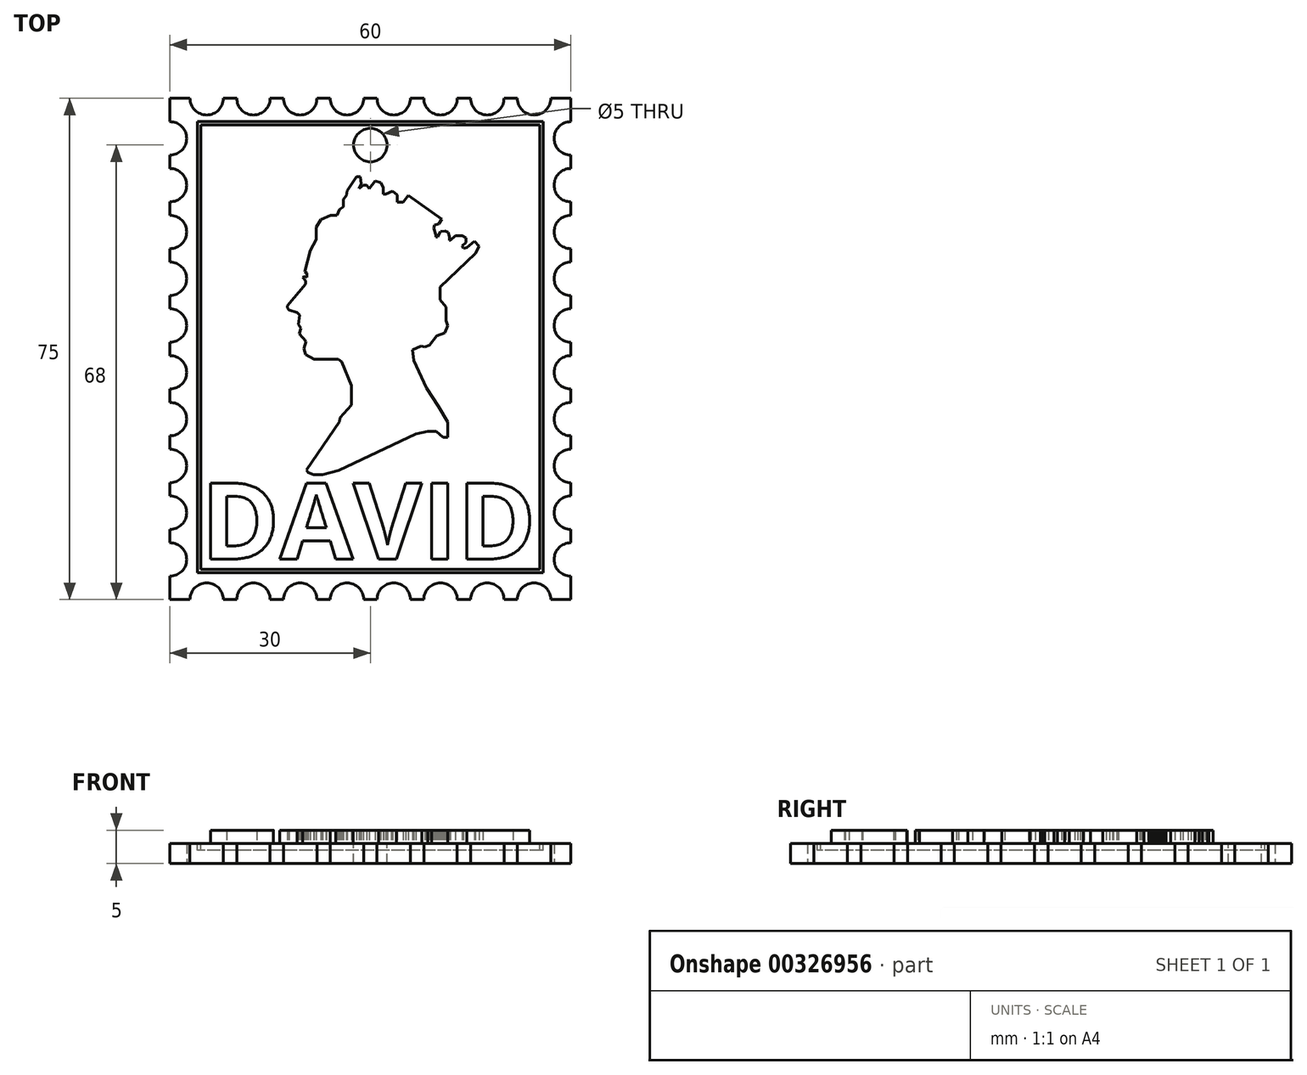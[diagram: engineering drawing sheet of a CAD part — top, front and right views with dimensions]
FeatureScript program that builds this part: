
annotation { "Feature Type Name" : "Feature", "Feature Type Description" : "" }
export const myFeature = defineFeature(function(context is Context, id is Id, definition is map)
    precondition{}
    {
        {
            var Q0;
            Q0=qCreatedBy(makeId("Top.planeOp"),FACE);
            var sketch = newSketch(context, id + "F0", { "sketchPlane" : qUnion([Q0])});
            skLineSegment(sketch, "E0.bottom", {"start": v(30, 37.5) * mm, "end": v(27, 37.5) * mm});
            skLineSegment(sketch, "E0.top", {"start": v(30, -37.5) * mm, "end": v(27, -37.5) * mm});
            skLineSegment(sketch, "E0.left", {"start": v(30, 37.5) * mm, "end": v(30, 34) * mm});
            skLineSegment(sketch, "E0.right", {"start": v(-30, 37.5) * mm, "end": v(-30, 34) * mm});
            skPoint(sketch, "E0.middle", {"position": v(0, 0) * mm});
            skArc(sketch, "E1", {"start": v(-27, 37.5) * mm, "mid": v(-24.5, 35) * mm, "end": v(-22, 37.5) * mm});
            skArc(sketch, "E2.1.0.0", {"start": v(-20, 37.5) * mm, "mid": v(-17.5, 35) * mm, "end": v(-15, 37.5) * mm});
            skArc(sketch, "E2.2.0.0", {"start": v(-13, 37.5) * mm, "mid": v(-10.5, 35) * mm, "end": v(-8, 37.5) * mm});
            skArc(sketch, "E2.3.0.0", {"start": v(-6, 37.5) * mm, "mid": v(-3.5, 35) * mm, "end": v(-1, 37.5) * mm});
            skArc(sketch, "E2.4.0.0", {"start": v(1, 37.5) * mm, "mid": v(3.5, 35) * mm, "end": v(6, 37.5) * mm});
            skArc(sketch, "E2.5.0.0", {"start": v(8, 37.5) * mm, "mid": v(10.5, 35) * mm, "end": v(13, 37.5) * mm});
            skArc(sketch, "E2.6.0.0", {"start": v(15, 37.5) * mm, "mid": v(17.5, 35) * mm, "end": v(20, 37.5) * mm});
            skArc(sketch, "E2.7.0.0", {"start": v(22, 37.5) * mm, "mid": v(24.5, 35) * mm, "end": v(27, 37.5) * mm});
            skLineSegment(sketch, "E2.direction1", {"start": v(-22, 37.5) * mm, "end": v(-20, 37.5) * mm, "construction": true});
            skArc(sketch, "E3", {"start": v(-30, 29) * mm, "mid": v(-27.5, 31.5) * mm, "end": v(-30, 34) * mm});
            skArc(sketch, "E4.0.1.0", {"start": v(-30, 22) * mm, "mid": v(-27.5, 24.5) * mm, "end": v(-30, 27) * mm});
            skArc(sketch, "E4.0.2.0", {"start": v(-30, 15) * mm, "mid": v(-27.5, 17.5) * mm, "end": v(-30, 20) * mm});
            skArc(sketch, "E4.0.3.0", {"start": v(-30, 8) * mm, "mid": v(-27.5, 10.5) * mm, "end": v(-30, 13) * mm});
            skArc(sketch, "E4.0.4.0", {"start": v(-30, 1) * mm, "mid": v(-27.5, 3.5) * mm, "end": v(-30, 6) * mm});
            skArc(sketch, "E4.0.5.0", {"start": v(-30, -6) * mm, "mid": v(-27.5, -3.5) * mm, "end": v(-30, -1) * mm});
            skArc(sketch, "E4.0.6.0", {"start": v(-30, -13) * mm, "mid": v(-27.5, -10.5) * mm, "end": v(-30, -8) * mm});
            skArc(sketch, "E4.0.7.0", {"start": v(-30, -20) * mm, "mid": v(-27.5, -17.5) * mm, "end": v(-30, -15) * mm});
            skArc(sketch, "E4.0.8.0", {"start": v(-30, -27) * mm, "mid": v(-27.5, -24.5) * mm, "end": v(-30, -22) * mm});
            skArc(sketch, "E4.0.9.0", {"start": v(-30, -34) * mm, "mid": v(-27.5, -31.5) * mm, "end": v(-30, -29) * mm});
            skArc(sketch, "E4.1.1.0", {"start": v(-30, 22) * mm, "mid": v(-27.5, 24.5) * mm, "end": v(-30, 27) * mm});
            skArc(sketch, "E4.1.2.0", {"start": v(-30, 15) * mm, "mid": v(-27.5, 17.5) * mm, "end": v(-30, 20) * mm});
            skArc(sketch, "E4.1.3.0", {"start": v(-30, 8) * mm, "mid": v(-27.5, 10.5) * mm, "end": v(-30, 13) * mm});
            skArc(sketch, "E4.1.4.0", {"start": v(-30, 1) * mm, "mid": v(-27.5, 3.5) * mm, "end": v(-30, 6) * mm});
            skArc(sketch, "E4.1.5.0", {"start": v(-30, -6) * mm, "mid": v(-27.5, -3.5) * mm, "end": v(-30, -1) * mm});
            skArc(sketch, "E4.1.6.0", {"start": v(-30, -13) * mm, "mid": v(-27.5, -10.5) * mm, "end": v(-30, -8) * mm});
            skArc(sketch, "E4.1.7.0", {"start": v(-30, -20) * mm, "mid": v(-27.5, -17.5) * mm, "end": v(-30, -15) * mm});
            skArc(sketch, "E4.1.8.0", {"start": v(-30, -27) * mm, "mid": v(-27.5, -24.5) * mm, "end": v(-30, -22) * mm});
            skArc(sketch, "E4.1.9.0", {"start": v(-30, -34) * mm, "mid": v(-27.5, -31.5) * mm, "end": v(-30, -29) * mm});
            skArc(sketch, "E4.2.1.0", {"start": v(-30, 22) * mm, "mid": v(-27.5, 24.5) * mm, "end": v(-30, 27) * mm});
            skArc(sketch, "E4.2.2.0", {"start": v(-30, 15) * mm, "mid": v(-27.5, 17.5) * mm, "end": v(-30, 20) * mm});
            skArc(sketch, "E4.2.3.0", {"start": v(-30, 8) * mm, "mid": v(-27.5, 10.5) * mm, "end": v(-30, 13) * mm});
            skArc(sketch, "E4.2.4.0", {"start": v(-30, 1) * mm, "mid": v(-27.5, 3.5) * mm, "end": v(-30, 6) * mm});
            skArc(sketch, "E4.2.5.0", {"start": v(-30, -6) * mm, "mid": v(-27.5, -3.5) * mm, "end": v(-30, -1) * mm});
            skArc(sketch, "E4.2.6.0", {"start": v(-30, -13) * mm, "mid": v(-27.5, -10.5) * mm, "end": v(-30, -8) * mm});
            skArc(sketch, "E4.2.7.0", {"start": v(-30, -20) * mm, "mid": v(-27.5, -17.5) * mm, "end": v(-30, -15) * mm});
            skArc(sketch, "E4.2.9.0", {"start": v(-30, -34) * mm, "mid": v(-27.5, -31.5) * mm, "end": v(-30, -29) * mm});
            skLineSegment(sketch, "E4.direction1", {"start": v(-30, 31.5) * mm, "end": v(-30, 31.5) * mm});
            skLineSegment(sketch, "E4.direction2", {"start": v(-30, 29) * mm, "end": v(-30, 27) * mm, "construction": true});
            skLineSegment(sketch, "E5.trimOffspring", {"start": v(-27, 37.5) * mm, "end": v(-30, 37.5) * mm});
            skLineSegment(sketch, "E6.trimOffspring", {"start": v(-20, 37.5) * mm, "end": v(-22, 37.5) * mm});
            skLineSegment(sketch, "E7.trimOffspring", {"start": v(-13, 37.5) * mm, "end": v(-15, 37.5) * mm});
            skLineSegment(sketch, "E8.trimOffspring", {"start": v(-6, 37.5) * mm, "end": v(-8, 37.5) * mm});
            skLineSegment(sketch, "E9.trimOffspring", {"start": v(1, 37.5) * mm, "end": v(-1, 37.5) * mm});
            skLineSegment(sketch, "E10.trimOffspring", {"start": v(8, 37.5) * mm, "end": v(6, 37.5) * mm});
            skLineSegment(sketch, "E11.trimOffspring", {"start": v(15, 37.5) * mm, "end": v(13, 37.5) * mm});
            skLineSegment(sketch, "E12.trimOffspring", {"start": v(22, 37.5) * mm, "end": v(20, 37.5) * mm});
            skLineSegment(sketch, "E13.trimOffspring", {"start": v(-30, 29) * mm, "end": v(-30, 24.5) * mm});
            skLineSegment(sketch, "E14.trimOffspring", {"start": v(-30, 22) * mm, "end": v(-30, 20) * mm});
            skLineSegment(sketch, "E15.trimOffspring", {"start": v(-30, 15) * mm, "end": v(-30, 13) * mm});
            skLineSegment(sketch, "E16.trimOffspring", {"start": v(-30, 8) * mm, "end": v(-30, 6) * mm});
            skLineSegment(sketch, "E17.trimOffspring", {"start": v(-30, 1) * mm, "end": v(-30, -1) * mm});
            skLineSegment(sketch, "E18.trimOffspring", {"start": v(-30, -6) * mm, "end": v(-30, -8) * mm});
            skLineSegment(sketch, "E19.trimOffspring", {"start": v(-30, -34) * mm, "end": v(-30, -37.5) * mm});
            skLineSegment(sketch, "E20.trimOffspring", {"start": v(-30, -27) * mm, "end": v(-30, -29) * mm});
            skLineSegment(sketch, "E21.trimOffspring", {"start": v(-30, -20) * mm, "end": v(-30, -22) * mm});
            skLineSegment(sketch, "E22.trimOffspring", {"start": v(-30, -13) * mm, "end": v(-30, -15) * mm});
            skArc(sketch, "E23.MirrorCS", {"start": v(-27, -37.5) * mm, "mid": v(-24.5, -35) * mm, "end": v(-22, -37.5) * mm});
            skArc(sketch, "E24.MirrorCS", {"start": v(-20, -37.5) * mm, "mid": v(-17.5, -35) * mm, "end": v(-15, -37.5) * mm});
            skArc(sketch, "E25.MirrorCS", {"start": v(-13, -37.5) * mm, "mid": v(-10.5, -35) * mm, "end": v(-8, -37.5) * mm});
            skArc(sketch, "E26.MirrorCS", {"start": v(1, -37.5) * mm, "mid": v(3.5, -35) * mm, "end": v(6, -37.5) * mm});
            skArc(sketch, "E27.MirrorCS", {"start": v(8, -37.5) * mm, "mid": v(10.5, -35) * mm, "end": v(13, -37.5) * mm});
            skArc(sketch, "E28.MirrorCS", {"start": v(-6, -37.5) * mm, "mid": v(-3.5, -35) * mm, "end": v(-1, -37.5) * mm});
            skArc(sketch, "E29.MirrorCS", {"start": v(15, -37.5) * mm, "mid": v(17.5, -35) * mm, "end": v(20, -37.5) * mm});
            skArc(sketch, "E30.MirrorCS", {"start": v(22, -37.5) * mm, "mid": v(24.5, -35) * mm, "end": v(27, -37.5) * mm});
            skLineSegment(sketch, "E31.trimOffspring", {"start": v(-27, -37.5) * mm, "end": v(-30, -37.5) * mm});
            skLineSegment(sketch, "E32.trimOffspring", {"start": v(-20, -37.5) * mm, "end": v(-22, -37.5) * mm});
            skLineSegment(sketch, "E33.trimOffspring", {"start": v(-13, -37.5) * mm, "end": v(-15, -37.5) * mm});
            skLineSegment(sketch, "E34.trimOffspring", {"start": v(-6, -37.5) * mm, "end": v(-8, -37.5) * mm});
            skLineSegment(sketch, "E35.trimOffspring", {"start": v(1, -37.5) * mm, "end": v(-1, -37.5) * mm});
            skLineSegment(sketch, "E36.trimOffspring", {"start": v(8, -37.5) * mm, "end": v(6, -37.5) * mm});
            skLineSegment(sketch, "E37.trimOffspring", {"start": v(15, -37.5) * mm, "end": v(13, -37.5) * mm});
            skLineSegment(sketch, "E38.trimOffspring", {"start": v(22, -37.5) * mm, "end": v(20, -37.5) * mm});
            skArc(sketch, "E39.MirrorCS", {"start": v(30, 29) * mm, "mid": v(27.5, 31.5) * mm, "end": v(30, 34) * mm});
            skArc(sketch, "E40.MirrorCS", {"start": v(30, 22) * mm, "mid": v(27.5, 24.5) * mm, "end": v(30, 27) * mm});
            skArc(sketch, "E41.MirrorCS", {"start": v(30, 15) * mm, "mid": v(27.5, 17.5) * mm, "end": v(30, 20) * mm});
            skArc(sketch, "E42.MirrorCS", {"start": v(30, 8) * mm, "mid": v(27.5, 10.5) * mm, "end": v(30, 13) * mm});
            skArc(sketch, "E43.MirrorCS", {"start": v(30, 1) * mm, "mid": v(27.5, 3.5) * mm, "end": v(30, 6) * mm});
            skArc(sketch, "E44.MirrorCS", {"start": v(30, -6) * mm, "mid": v(27.5, -3.5) * mm, "end": v(30, -1) * mm});
            skArc(sketch, "E45.MirrorCS", {"start": v(30, -13) * mm, "mid": v(27.5, -10.5) * mm, "end": v(30, -8) * mm});
            skArc(sketch, "E46.MirrorCS", {"start": v(30, -20) * mm, "mid": v(27.5, -17.5) * mm, "end": v(30, -15) * mm});
            skArc(sketch, "E47.MirrorCS", {"start": v(30, -27) * mm, "mid": v(27.5, -24.5) * mm, "end": v(30, -22) * mm});
            skArc(sketch, "E48.MirrorCS", {"start": v(30, -34) * mm, "mid": v(27.5, -31.5) * mm, "end": v(30, -29) * mm});
            skLineSegment(sketch, "E49.trimOffspring", {"start": v(30, 29) * mm, "end": v(30, 27) * mm});
            skLineSegment(sketch, "E50.trimOffspring", {"start": v(30, 22) * mm, "end": v(30, 20) * mm});
            skLineSegment(sketch, "E51.trimOffspring", {"start": v(30, 15) * mm, "end": v(30, 13) * mm});
            skLineSegment(sketch, "E52.trimOffspring", {"start": v(30, 8) * mm, "end": v(30, 6) * mm});
            skLineSegment(sketch, "E53.trimOffspring", {"start": v(30, 1) * mm, "end": v(30, -1) * mm});
            skLineSegment(sketch, "E54.trimOffspring", {"start": v(30, -6) * mm, "end": v(30, -8) * mm});
            skLineSegment(sketch, "E55.trimOffspring", {"start": v(30, -34) * mm, "end": v(30, -37.5) * mm});
            skLineSegment(sketch, "E56.trimOffspring", {"start": v(30, -27) * mm, "end": v(30, -29) * mm});
            skLineSegment(sketch, "E57.trimOffspring", {"start": v(30, -20) * mm, "end": v(30, -22) * mm});
            skLineSegment(sketch, "E58.trimOffspring", {"start": v(30, -13) * mm, "end": v(30, -15) * mm});
            skSolve(sketch);
        }
        {
            var Q0;
            Q0=makeQuery(id+"F0.imprint","IMPRINT",FACE,{"disambiguationData":[TD([[makeQuery(id+"F0.imprint","IMPRINT",EDGE,{"derivedFrom":sQuery(id+"F0.wireOp",EDGE,"E0.bottom")}),1.0]])]});
            extrude(context, id + "F1", {"entities" : qUnion([Q0]), "depth" : 3 * mm});
        }
        {
            var Q0;
            Q0=makeQuery(id+"F1.opExtrude","CAP_FACE",FACE,{"disambiguationData":[OSD([sQuery(id+"F0.wireOp",EDGE,"E0.bottom"),sQuery(id+"F0.wireOp",EDGE,"E0.top"),sQuery(id+"F0.wireOp",EDGE,"E0.left"),sQuery(id+"F0.wireOp",EDGE,"E0.right"),sQuery(id+"F0.wireOp",EDGE,"E1"),sQuery(id+"F0.wireOp",EDGE,"E2.1.0.0"),sQuery(id+"F0.wireOp",EDGE,"E2.2.0.0"),sQuery(id+"F0.wireOp",EDGE,"E2.3.0.0"),sQuery(id+"F0.wireOp",EDGE,"E2.4.0.0"),sQuery(id+"F0.wireOp",EDGE,"E2.5.0.0"),sQuery(id+"F0.wireOp",EDGE,"E2.6.0.0"),sQuery(id+"F0.wireOp",EDGE,"E2.7.0.0"),sQuery(id+"F0.wireOp",EDGE,"E4.1.8.0"),sQuery(id+"F0.wireOp",EDGE,"E3"),sQuery(id+"F0.wireOp",EDGE,"E4.2.1.0"),sQuery(id+"F0.wireOp",EDGE,"E4.2.2.0"),sQuery(id+"F0.wireOp",EDGE,"E4.2.3.0"),sQuery(id+"F0.wireOp",EDGE,"E4.2.4.0"),sQuery(id+"F0.wireOp",EDGE,"E4.2.5.0"),sQuery(id+"F0.wireOp",EDGE,"E4.2.6.0"),sQuery(id+"F0.wireOp",EDGE,"E4.2.7.0"),sQuery(id+"F0.wireOp",EDGE,"E4.2.9.0"),sQuery(id+"F0.wireOp",EDGE,"E5.trimOffspring"),sQuery(id+"F0.wireOp",EDGE,"E6.trimOffspring"),sQuery(id+"F0.wireOp",EDGE,"E7.trimOffspring"),sQuery(id+"F0.wireOp",EDGE,"E8.trimOffspring"),sQuery(id+"F0.wireOp",EDGE,"E9.trimOffspring"),sQuery(id+"F0.wireOp",EDGE,"E10.trimOffspring"),sQuery(id+"F0.wireOp",EDGE,"E11.trimOffspring"),sQuery(id+"F0.wireOp",EDGE,"E12.trimOffspring"),sQuery(id+"F0.wireOp",EDGE,"E13.trimOffspring"),sQuery(id+"F0.wireOp",EDGE,"E14.trimOffspring"),sQuery(id+"F0.wireOp",EDGE,"E15.trimOffspring"),sQuery(id+"F0.wireOp",EDGE,"E16.trimOffspring"),sQuery(id+"F0.wireOp",EDGE,"E17.trimOffspring"),sQuery(id+"F0.wireOp",EDGE,"E18.trimOffspring"),sQuery(id+"F0.wireOp",EDGE,"E19.trimOffspring"),sQuery(id+"F0.wireOp",EDGE,"E20.trimOffspring"),sQuery(id+"F0.wireOp",EDGE,"E21.trimOffspring"),sQuery(id+"F0.wireOp",EDGE,"E22.trimOffspring"),sQuery(id+"F0.wireOp",EDGE,"E23.MirrorCS"),sQuery(id+"F0.wireOp",EDGE,"E24.MirrorCS"),sQuery(id+"F0.wireOp",EDGE,"E25.MirrorCS"),sQuery(id+"F0.wireOp",EDGE,"E26.MirrorCS"),sQuery(id+"F0.wireOp",EDGE,"E27.MirrorCS"),sQuery(id+"F0.wireOp",EDGE,"E28.MirrorCS"),sQuery(id+"F0.wireOp",EDGE,"E29.MirrorCS"),sQuery(id+"F0.wireOp",EDGE,"E30.MirrorCS"),sQuery(id+"F0.wireOp",EDGE,"E31.trimOffspring"),sQuery(id+"F0.wireOp",EDGE,"E32.trimOffspring"),sQuery(id+"F0.wireOp",EDGE,"E33.trimOffspring"),sQuery(id+"F0.wireOp",EDGE,"E34.trimOffspring"),sQuery(id+"F0.wireOp",EDGE,"E35.trimOffspring"),sQuery(id+"F0.wireOp",EDGE,"E36.trimOffspring"),sQuery(id+"F0.wireOp",EDGE,"E37.trimOffspring"),sQuery(id+"F0.wireOp",EDGE,"E38.trimOffspring"),sQuery(id+"F0.wireOp",EDGE,"E39.MirrorCS"),sQuery(id+"F0.wireOp",EDGE,"E40.MirrorCS"),sQuery(id+"F0.wireOp",EDGE,"E41.MirrorCS"),sQuery(id+"F0.wireOp",EDGE,"E42.MirrorCS"),sQuery(id+"F0.wireOp",EDGE,"E43.MirrorCS"),sQuery(id+"F0.wireOp",EDGE,"E44.MirrorCS"),sQuery(id+"F0.wireOp",EDGE,"E45.MirrorCS"),sQuery(id+"F0.wireOp",EDGE,"E46.MirrorCS"),sQuery(id+"F0.wireOp",EDGE,"E47.MirrorCS"),sQuery(id+"F0.wireOp",EDGE,"E48.MirrorCS"),sQuery(id+"F0.wireOp",EDGE,"E49.trimOffspring"),sQuery(id+"F0.wireOp",EDGE,"E50.trimOffspring"),sQuery(id+"F0.wireOp",EDGE,"E51.trimOffspring"),sQuery(id+"F0.wireOp",EDGE,"E52.trimOffspring"),sQuery(id+"F0.wireOp",EDGE,"E53.trimOffspring"),sQuery(id+"F0.wireOp",EDGE,"E54.trimOffspring"),sQuery(id+"F0.wireOp",EDGE,"E55.trimOffspring"),sQuery(id+"F0.wireOp",EDGE,"E56.trimOffspring"),sQuery(id+"F0.wireOp",EDGE,"E57.trimOffspring"),sQuery(id+"F0.wireOp",EDGE,"E58.trimOffspring")])],"isStart":false});
            var sketch = newSketch(context, id + "F2", { "sketchPlane" : qUnion([Q0])});
            skText(sketch, "E59", { "text": "DAVID", "fontName": "OpenSans-Bold.ttf"});
            skPoint(sketch, "E60", {"position": v(27.5, -31.5) * mm});
            const initialGuessF2  = {"E59": [-0.02535, -0.03145, 1, 0, 0.01145]};
            skSetInitialGuess(sketch, initialGuessF2);
            skSolve(sketch);
        }
        {
            var Q0;
            Q0=makeQuery(id+"F2.imprint","IMPRINT",FACE,{"disambiguationData":[TD([[makeQuery(id+"F2.imprint","IMPRINT",EDGE,{"derivedFrom":sQuery(id+"F2.wireOp",EDGE,"E59.sketch_text.stroke-0")}),-1.0]])]});
            var Q1;
            Q1=makeQuery(id+"F2.imprint","IMPRINT",FACE,{"disambiguationData":[TD([[makeQuery(id+"F2.imprint","IMPRINT",EDGE,{"derivedFrom":sQuery(id+"F2.wireOp",EDGE,"E59.sketch_text.stroke-12")}),-1.0]])]});
            var Q2;
            Q2=makeQuery(id+"F2.imprint","IMPRINT",FACE,{"disambiguationData":[TD([[makeQuery(id+"F2.imprint","IMPRINT",EDGE,{"derivedFrom":sQuery(id+"F2.wireOp",EDGE,"E59.sketch_text.stroke-24")}),-1.0]])]});
            var Q3;
            Q3=makeQuery(id+"F2.imprint","IMPRINT",FACE,{"disambiguationData":[TD([[makeQuery(id+"F2.imprint","IMPRINT",EDGE,{"derivedFrom":sQuery(id+"F2.wireOp",EDGE,"E59.sketch_text.stroke-34")}),-1.0]])]});
            var Q4;
            Q4=makeQuery(id+"F2.imprint","IMPRINT",FACE,{"disambiguationData":[TD([[makeQuery(id+"F2.imprint","IMPRINT",EDGE,{"derivedFrom":sQuery(id+"F2.wireOp",EDGE,"E59.sketch_text.stroke-38")}),-1.0]])]});
            extrude(context, id + "F3", {"entities" : qUnion([Q0, Q1, Q2, Q3, Q4]), "operationType" : NewBodyOperationType.ADD, "depth" : 2 * mm});
        }
        {
            var Q0;
            {var subQ0=sQuery(id+"F0.wireOp",EDGE,"E58.trimOffspring");var subQ1=sQuery(id+"F0.wireOp",EDGE,"E57.trimOffspring");var subQ2=sQuery(id+"F0.wireOp",EDGE,"E56.trimOffspring");var subQ3=sQuery(id+"F0.wireOp",EDGE,"E55.trimOffspring");var subQ4=sQuery(id+"F0.wireOp",EDGE,"E54.trimOffspring");var subQ5=sQuery(id+"F0.wireOp",EDGE,"E53.trimOffspring");var subQ6=sQuery(id+"F0.wireOp",EDGE,"E52.trimOffspring");var subQ7=sQuery(id+"F0.wireOp",EDGE,"E51.trimOffspring");var subQ8=sQuery(id+"F0.wireOp",EDGE,"E50.trimOffspring");var subQ9=sQuery(id+"F0.wireOp",EDGE,"E49.trimOffspring");var subQ10=sQuery(id+"F0.wireOp",EDGE,"E48.MirrorCS");var subQ11=sQuery(id+"F0.wireOp",EDGE,"E47.MirrorCS");var subQ12=sQuery(id+"F0.wireOp",EDGE,"E46.MirrorCS");var subQ13=sQuery(id+"F0.wireOp",EDGE,"E45.MirrorCS");var subQ14=sQuery(id+"F0.wireOp",EDGE,"E44.MirrorCS");var subQ15=sQuery(id+"F0.wireOp",EDGE,"E43.MirrorCS");var subQ16=sQuery(id+"F0.wireOp",EDGE,"E42.MirrorCS");var subQ17=sQuery(id+"F0.wireOp",EDGE,"E41.MirrorCS");var subQ18=sQuery(id+"F0.wireOp",EDGE,"E40.MirrorCS");var subQ19=sQuery(id+"F0.wireOp",EDGE,"E39.MirrorCS");var subQ20=sQuery(id+"F0.wireOp",EDGE,"E38.trimOffspring");var subQ21=sQuery(id+"F0.wireOp",EDGE,"E37.trimOffspring");var subQ22=sQuery(id+"F0.wireOp",EDGE,"E36.trimOffspring");var subQ23=sQuery(id+"F0.wireOp",EDGE,"E35.trimOffspring");var subQ24=sQuery(id+"F0.wireOp",EDGE,"E34.trimOffspring");var subQ25=sQuery(id+"F0.wireOp",EDGE,"E33.trimOffspring");var subQ26=sQuery(id+"F0.wireOp",EDGE,"E32.trimOffspring");var subQ27=sQuery(id+"F0.wireOp",EDGE,"E31.trimOffspring");var subQ28=sQuery(id+"F0.wireOp",EDGE,"E30.MirrorCS");var subQ29=sQuery(id+"F0.wireOp",EDGE,"E29.MirrorCS");var subQ30=sQuery(id+"F0.wireOp",EDGE,"E12.trimOffspring");var subQ31=sQuery(id+"F0.wireOp",EDGE,"E4.2.7.0");var subQ32=sQuery(id+"F0.wireOp",EDGE,"E11.trimOffspring");var subQ33=sQuery(id+"F0.wireOp",EDGE,"E4.2.6.0");var subQ34=sQuery(id+"F0.wireOp",EDGE,"E4.2.5.0");var subQ35=sQuery(id+"F0.wireOp",EDGE,"E4.2.4.0");var subQ36=sQuery(id+"F0.wireOp",EDGE,"E8.trimOffspring");var subQ37=sQuery(id+"F0.wireOp",EDGE,"E4.2.3.0");var subQ38=sQuery(id+"F0.wireOp",EDGE,"E4.2.2.0");var subQ39=sQuery(id+"F0.wireOp",EDGE,"E4.2.1.0");var subQ40=sQuery(id+"F0.wireOp",EDGE,"E3");var subQ41=sQuery(id+"F0.wireOp",EDGE,"E4.1.8.0");var subQ42=sQuery(id+"F0.wireOp",EDGE,"E2.7.0.0");var subQ43=sQuery(id+"F0.wireOp",EDGE,"E2.6.0.0");var subQ44=sQuery(id+"F0.wireOp",EDGE,"E0.left");var subQ45=sQuery(id+"F0.wireOp",EDGE,"E0.top");var subQ46=sQuery(id+"F0.wireOp",EDGE,"E0.right");var subQ47=sQuery(id+"F0.wireOp",EDGE,"E13.trimOffspring");var subQ48=sQuery(id+"F0.wireOp",EDGE,"E4.2.9.0");var subQ49=sQuery(id+"F0.wireOp",EDGE,"E0.bottom");var subQ50=sQuery(id+"F0.wireOp",EDGE,"E28.MirrorCS");var subQ51=sQuery(id+"F0.wireOp",EDGE,"E2.5.0.0");var subQ52=sQuery(id+"F0.wireOp",EDGE,"E1");var subQ53=sQuery(id+"F0.wireOp",EDGE,"E2.1.0.0");var subQ54=sQuery(id+"F0.wireOp",EDGE,"E2.2.0.0");var subQ55=sQuery(id+"F0.wireOp",EDGE,"E2.3.0.0");var subQ56=sQuery(id+"F0.wireOp",EDGE,"E2.4.0.0");var subQ57=sQuery(id+"F0.wireOp",EDGE,"E14.trimOffspring");var subQ58=sQuery(id+"F0.wireOp",EDGE,"E5.trimOffspring");var subQ59=sQuery(id+"F0.wireOp",EDGE,"E15.trimOffspring");var subQ60=sQuery(id+"F0.wireOp",EDGE,"E6.trimOffspring");var subQ61=sQuery(id+"F0.wireOp",EDGE,"E16.trimOffspring");var subQ62=sQuery(id+"F0.wireOp",EDGE,"E7.trimOffspring");var subQ63=sQuery(id+"F0.wireOp",EDGE,"E9.trimOffspring");var subQ64=sQuery(id+"F0.wireOp",EDGE,"E10.trimOffspring");var subQ65=sQuery(id+"F0.wireOp",EDGE,"E22.trimOffspring");var subQ66=sQuery(id+"F0.wireOp",EDGE,"E25.MirrorCS");var subQ67=sQuery(id+"F0.wireOp",EDGE,"E26.MirrorCS");var subQ68=sQuery(id+"F0.wireOp",EDGE,"E17.trimOffspring");var subQ69=sQuery(id+"F0.wireOp",EDGE,"E27.MirrorCS");var subQ70=sQuery(id+"F0.wireOp",EDGE,"E18.trimOffspring");var subQ71=sQuery(id+"F0.wireOp",EDGE,"E19.trimOffspring");var subQ72=sQuery(id+"F0.wireOp",EDGE,"E20.trimOffspring");var subQ73=sQuery(id+"F0.wireOp",EDGE,"E21.trimOffspring");var subQ74=sQuery(id+"F0.wireOp",EDGE,"E23.MirrorCS");var subQ75=sQuery(id+"F0.wireOp",EDGE,"E24.MirrorCS");Q0=makeQuery(id+"F3.boolean.opBoolean","SPLIT",FACE,{"disambiguationData":[TD([makeQuery(id+"F1.opExtrude","SWEPT_FACE",FACE,{"disambiguationData":[OSD([subQ49])]})])],"derivedFrom":makeQuery(id+"F1.opExtrude","CAP_FACE",FACE,{"disambiguationData":[OSD([subQ49,subQ45,subQ44,subQ46,subQ52,subQ53,subQ54,subQ55,subQ56,subQ51,subQ43,subQ42,subQ41,subQ40,subQ39,subQ38,subQ37,subQ35,subQ34,subQ33,subQ31,subQ48,subQ58,subQ60,subQ62,subQ36,subQ63,subQ64,subQ32,subQ30,subQ47,subQ57,subQ59,subQ61,subQ68,subQ70,subQ71,subQ72,subQ73,subQ65,subQ74,subQ75,subQ66,subQ67,subQ69,subQ50,subQ29,subQ28,subQ27,subQ26,subQ25,subQ24,subQ23,subQ22,subQ21,subQ20,subQ19,subQ18,subQ17,subQ16,subQ15,subQ14,subQ13,subQ12,subQ11,subQ10,subQ9,subQ8,subQ7,subQ6,subQ5,subQ4,subQ3,subQ2,subQ1,subQ0])],"isStart":false})});}
            var sketch = newSketch(context, id + "F4", { "sketchPlane" : qUnion([Q0])});
            skCircle(sketch, "E61", {"center": v(0, 30.5) * mm, "radius": 2.5 * mm});
            skSolve(sketch);
        }
        {
            var Q0;
            Q0=makeQuery(id+"F4.imprint","IMPRINT",FACE,{"disambiguationData":[TD([[makeQuery(id+"F4.imprint","IMPRINT",EDGE,{"derivedFrom":sQuery(id+"F4.wireOp",EDGE,"E61")}),1.0]])]});
            extrude(context, id + "F5", {"entities" : qUnion([Q0]), "operationType" : NewBodyOperationType.REMOVE, "endBound" : BoundingType.THROUGH_ALL, "oppositeDirection" : true, "depth" : 25 * mm});
        }
        {
            var Q0;
            {var subQ0=sQuery(id+"F0.wireOp",EDGE,"E58.trimOffspring");var subQ1=sQuery(id+"F0.wireOp",EDGE,"E57.trimOffspring");var subQ2=sQuery(id+"F0.wireOp",EDGE,"E56.trimOffspring");var subQ3=sQuery(id+"F0.wireOp",EDGE,"E55.trimOffspring");var subQ4=sQuery(id+"F0.wireOp",EDGE,"E54.trimOffspring");var subQ5=sQuery(id+"F0.wireOp",EDGE,"E53.trimOffspring");var subQ6=sQuery(id+"F0.wireOp",EDGE,"E52.trimOffspring");var subQ7=sQuery(id+"F0.wireOp",EDGE,"E51.trimOffspring");var subQ8=sQuery(id+"F0.wireOp",EDGE,"E50.trimOffspring");var subQ9=sQuery(id+"F0.wireOp",EDGE,"E49.trimOffspring");var subQ10=sQuery(id+"F0.wireOp",EDGE,"E48.MirrorCS");var subQ11=sQuery(id+"F0.wireOp",EDGE,"E47.MirrorCS");var subQ12=sQuery(id+"F0.wireOp",EDGE,"E46.MirrorCS");var subQ13=sQuery(id+"F0.wireOp",EDGE,"E45.MirrorCS");var subQ14=sQuery(id+"F0.wireOp",EDGE,"E44.MirrorCS");var subQ15=sQuery(id+"F0.wireOp",EDGE,"E43.MirrorCS");var subQ16=sQuery(id+"F0.wireOp",EDGE,"E42.MirrorCS");var subQ17=sQuery(id+"F0.wireOp",EDGE,"E41.MirrorCS");var subQ18=sQuery(id+"F0.wireOp",EDGE,"E40.MirrorCS");var subQ19=sQuery(id+"F0.wireOp",EDGE,"E39.MirrorCS");var subQ20=sQuery(id+"F0.wireOp",EDGE,"E38.trimOffspring");var subQ21=sQuery(id+"F0.wireOp",EDGE,"E37.trimOffspring");var subQ22=sQuery(id+"F0.wireOp",EDGE,"E36.trimOffspring");var subQ23=sQuery(id+"F0.wireOp",EDGE,"E35.trimOffspring");var subQ24=sQuery(id+"F0.wireOp",EDGE,"E34.trimOffspring");var subQ25=sQuery(id+"F0.wireOp",EDGE,"E33.trimOffspring");var subQ26=sQuery(id+"F0.wireOp",EDGE,"E32.trimOffspring");var subQ27=sQuery(id+"F0.wireOp",EDGE,"E31.trimOffspring");var subQ28=sQuery(id+"F0.wireOp",EDGE,"E30.MirrorCS");var subQ29=sQuery(id+"F0.wireOp",EDGE,"E29.MirrorCS");var subQ30=sQuery(id+"F0.wireOp",EDGE,"E12.trimOffspring");var subQ31=sQuery(id+"F0.wireOp",EDGE,"E4.2.7.0");var subQ32=sQuery(id+"F0.wireOp",EDGE,"E11.trimOffspring");var subQ33=sQuery(id+"F0.wireOp",EDGE,"E4.2.6.0");var subQ34=sQuery(id+"F0.wireOp",EDGE,"E4.2.5.0");var subQ35=sQuery(id+"F0.wireOp",EDGE,"E4.2.4.0");var subQ36=sQuery(id+"F0.wireOp",EDGE,"E8.trimOffspring");var subQ37=sQuery(id+"F0.wireOp",EDGE,"E4.2.3.0");var subQ38=sQuery(id+"F0.wireOp",EDGE,"E4.2.2.0");var subQ39=sQuery(id+"F0.wireOp",EDGE,"E4.2.1.0");var subQ40=sQuery(id+"F0.wireOp",EDGE,"E3");var subQ41=sQuery(id+"F0.wireOp",EDGE,"E4.1.8.0");var subQ42=sQuery(id+"F0.wireOp",EDGE,"E2.7.0.0");var subQ43=sQuery(id+"F0.wireOp",EDGE,"E2.6.0.0");var subQ44=sQuery(id+"F0.wireOp",EDGE,"E0.left");var subQ45=sQuery(id+"F0.wireOp",EDGE,"E0.top");var subQ46=sQuery(id+"F0.wireOp",EDGE,"E0.right");var subQ47=sQuery(id+"F0.wireOp",EDGE,"E13.trimOffspring");var subQ48=sQuery(id+"F0.wireOp",EDGE,"E4.2.9.0");var subQ49=sQuery(id+"F0.wireOp",EDGE,"E0.bottom");var subQ50=sQuery(id+"F0.wireOp",EDGE,"E28.MirrorCS");var subQ51=sQuery(id+"F0.wireOp",EDGE,"E2.5.0.0");var subQ52=sQuery(id+"F0.wireOp",EDGE,"E1");var subQ53=sQuery(id+"F0.wireOp",EDGE,"E2.1.0.0");var subQ54=sQuery(id+"F0.wireOp",EDGE,"E2.2.0.0");var subQ55=sQuery(id+"F0.wireOp",EDGE,"E2.3.0.0");var subQ56=sQuery(id+"F0.wireOp",EDGE,"E2.4.0.0");var subQ57=sQuery(id+"F0.wireOp",EDGE,"E14.trimOffspring");var subQ58=sQuery(id+"F0.wireOp",EDGE,"E5.trimOffspring");var subQ59=sQuery(id+"F0.wireOp",EDGE,"E15.trimOffspring");var subQ60=sQuery(id+"F0.wireOp",EDGE,"E6.trimOffspring");var subQ61=sQuery(id+"F0.wireOp",EDGE,"E16.trimOffspring");var subQ62=sQuery(id+"F0.wireOp",EDGE,"E7.trimOffspring");var subQ63=sQuery(id+"F0.wireOp",EDGE,"E9.trimOffspring");var subQ64=sQuery(id+"F0.wireOp",EDGE,"E10.trimOffspring");var subQ65=sQuery(id+"F0.wireOp",EDGE,"E22.trimOffspring");var subQ66=sQuery(id+"F0.wireOp",EDGE,"E25.MirrorCS");var subQ67=sQuery(id+"F0.wireOp",EDGE,"E26.MirrorCS");var subQ68=sQuery(id+"F0.wireOp",EDGE,"E17.trimOffspring");var subQ69=sQuery(id+"F0.wireOp",EDGE,"E27.MirrorCS");var subQ70=sQuery(id+"F0.wireOp",EDGE,"E18.trimOffspring");var subQ71=sQuery(id+"F0.wireOp",EDGE,"E19.trimOffspring");var subQ72=sQuery(id+"F0.wireOp",EDGE,"E20.trimOffspring");var subQ73=sQuery(id+"F0.wireOp",EDGE,"E21.trimOffspring");var subQ74=sQuery(id+"F0.wireOp",EDGE,"E23.MirrorCS");var subQ75=sQuery(id+"F0.wireOp",EDGE,"E24.MirrorCS");Q0=makeQuery(id+"F3.boolean.opBoolean","SPLIT",FACE,{"disambiguationData":[TD([makeQuery(id+"F1.opExtrude","SWEPT_FACE",FACE,{"disambiguationData":[OSD([subQ49])]})])],"derivedFrom":makeQuery(id+"F1.opExtrude","CAP_FACE",FACE,{"disambiguationData":[OSD([subQ49,subQ45,subQ44,subQ46,subQ52,subQ53,subQ54,subQ55,subQ56,subQ51,subQ43,subQ42,subQ41,subQ40,subQ39,subQ38,subQ37,subQ35,subQ34,subQ33,subQ31,subQ48,subQ58,subQ60,subQ62,subQ36,subQ63,subQ64,subQ32,subQ30,subQ47,subQ57,subQ59,subQ61,subQ68,subQ70,subQ71,subQ72,subQ73,subQ65,subQ74,subQ75,subQ66,subQ67,subQ69,subQ50,subQ29,subQ28,subQ27,subQ26,subQ25,subQ24,subQ23,subQ22,subQ21,subQ20,subQ19,subQ18,subQ17,subQ16,subQ15,subQ14,subQ13,subQ12,subQ11,subQ10,subQ9,subQ8,subQ7,subQ6,subQ5,subQ4,subQ3,subQ2,subQ1,subQ0])],"isStart":false})});}
            var sketch = newSketch(context, id + "F6", { "sketchPlane" : qUnion([Q0])});
            skLineSegment(sketch, "E62.bottom", {"start": v(25.86, 34) * mm, "end": v(-25.86, 34) * mm});
            skLineSegment(sketch, "E62.top", {"start": v(25.86, -33.5) * mm, "end": v(-25.86, -33.5) * mm});
            skLineSegment(sketch, "E62.left", {"start": v(25.86, 34) * mm, "end": v(25.86, -33.5) * mm});
            skLineSegment(sketch, "E62.right", {"start": v(-25.86, 34) * mm, "end": v(-25.86, -33.5) * mm});
            skPoint(sketch, "E62.middle", {"position": v(0, 0.25) * mm});
            skLineSegment(sketch, "E63.0", {"start": v(25.36, 33.5) * mm, "end": v(-25.36, 33.5) * mm});
            skLineSegment(sketch, "E64.0", {"start": v(25.36, 33.5) * mm, "end": v(25.36, -33) * mm});
            skLineSegment(sketch, "E65.0", {"start": v(25.36, -33) * mm, "end": v(-25.36, -33) * mm});
            skLineSegment(sketch, "E66.trimOffspring", {"start": v(-25.36, 33.5) * mm, "end": v(-25.36, -33) * mm});
            skSolve(sketch);
        }
        {
            var Q0;
            Q0=makeQuery(id+"F6.imprint","IMPRINT",FACE,{"disambiguationData":[TD([[makeQuery(id+"F6.imprint","IMPRINT",EDGE,{"derivedFrom":sQuery(id+"F6.wireOp",EDGE,"E62.bottom")}),1.0]])]});
            extrude(context, id + "F7", {"entities" : qUnion([Q0]), "operationType" : NewBodyOperationType.REMOVE, "oppositeDirection" : true, "depth" : 1 * mm});
        }
        {
            var Q0;
            {var subQ18=makeQuery(id+"F3.opExtrude","SWEPT_FACE",FACE,{"disambiguationData":[OSD([sQuery(id+"F2.wireOp",EDGE,"E59.sketch_text.stroke-0")])]});var subQ36=sQuery(id+"F0.wireOp",EDGE,"E58.trimOffspring");var subQ37=sQuery(id+"F0.wireOp",EDGE,"E57.trimOffspring");var subQ38=sQuery(id+"F0.wireOp",EDGE,"E56.trimOffspring");var subQ39=sQuery(id+"F0.wireOp",EDGE,"E55.trimOffspring");var subQ40=sQuery(id+"F0.wireOp",EDGE,"E54.trimOffspring");var subQ41=sQuery(id+"F0.wireOp",EDGE,"E53.trimOffspring");var subQ42=sQuery(id+"F0.wireOp",EDGE,"E52.trimOffspring");var subQ43=sQuery(id+"F0.wireOp",EDGE,"E51.trimOffspring");var subQ44=sQuery(id+"F0.wireOp",EDGE,"E50.trimOffspring");var subQ45=sQuery(id+"F0.wireOp",EDGE,"E49.trimOffspring");var subQ46=sQuery(id+"F0.wireOp",EDGE,"E48.MirrorCS");var subQ47=sQuery(id+"F0.wireOp",EDGE,"E47.MirrorCS");var subQ48=sQuery(id+"F0.wireOp",EDGE,"E46.MirrorCS");var subQ49=sQuery(id+"F0.wireOp",EDGE,"E45.MirrorCS");var subQ50=sQuery(id+"F0.wireOp",EDGE,"E44.MirrorCS");var subQ51=sQuery(id+"F0.wireOp",EDGE,"E43.MirrorCS");var subQ52=sQuery(id+"F0.wireOp",EDGE,"E42.MirrorCS");var subQ53=sQuery(id+"F0.wireOp",EDGE,"E41.MirrorCS");var subQ54=sQuery(id+"F0.wireOp",EDGE,"E40.MirrorCS");var subQ55=sQuery(id+"F0.wireOp",EDGE,"E39.MirrorCS");var subQ56=sQuery(id+"F0.wireOp",EDGE,"E38.trimOffspring");var subQ57=sQuery(id+"F0.wireOp",EDGE,"E37.trimOffspring");var subQ58=sQuery(id+"F0.wireOp",EDGE,"E36.trimOffspring");var subQ59=sQuery(id+"F0.wireOp",EDGE,"E35.trimOffspring");var subQ60=sQuery(id+"F0.wireOp",EDGE,"E34.trimOffspring");var subQ61=sQuery(id+"F0.wireOp",EDGE,"E33.trimOffspring");var subQ62=sQuery(id+"F0.wireOp",EDGE,"E32.trimOffspring");var subQ63=sQuery(id+"F0.wireOp",EDGE,"E31.trimOffspring");var subQ64=sQuery(id+"F0.wireOp",EDGE,"E30.MirrorCS");var subQ65=sQuery(id+"F0.wireOp",EDGE,"E29.MirrorCS");var subQ66=sQuery(id+"F0.wireOp",EDGE,"E12.trimOffspring");var subQ67=sQuery(id+"F0.wireOp",EDGE,"E4.2.7.0");var subQ68=sQuery(id+"F0.wireOp",EDGE,"E11.trimOffspring");var subQ69=sQuery(id+"F0.wireOp",EDGE,"E4.2.6.0");var subQ70=sQuery(id+"F0.wireOp",EDGE,"E4.2.5.0");var subQ71=sQuery(id+"F0.wireOp",EDGE,"E4.2.4.0");var subQ72=sQuery(id+"F0.wireOp",EDGE,"E8.trimOffspring");var subQ73=sQuery(id+"F0.wireOp",EDGE,"E4.2.3.0");var subQ74=sQuery(id+"F0.wireOp",EDGE,"E4.2.2.0");var subQ75=sQuery(id+"F0.wireOp",EDGE,"E4.2.1.0");var subQ76=sQuery(id+"F0.wireOp",EDGE,"E3");var subQ77=sQuery(id+"F0.wireOp",EDGE,"E4.1.8.0");var subQ78=sQuery(id+"F0.wireOp",EDGE,"E2.7.0.0");var subQ79=sQuery(id+"F0.wireOp",EDGE,"E2.6.0.0");var subQ80=sQuery(id+"F0.wireOp",EDGE,"E0.left");var subQ81=sQuery(id+"F0.wireOp",EDGE,"E0.top");var subQ82=sQuery(id+"F0.wireOp",EDGE,"E0.right");var subQ83=sQuery(id+"F0.wireOp",EDGE,"E13.trimOffspring");var subQ84=sQuery(id+"F0.wireOp",EDGE,"E4.2.9.0");var subQ85=sQuery(id+"F0.wireOp",EDGE,"E0.bottom");var subQ86=sQuery(id+"F0.wireOp",EDGE,"E28.MirrorCS");var subQ87=sQuery(id+"F0.wireOp",EDGE,"E2.5.0.0");var subQ88=sQuery(id+"F0.wireOp",EDGE,"E1");var subQ89=sQuery(id+"F0.wireOp",EDGE,"E2.1.0.0");var subQ90=sQuery(id+"F0.wireOp",EDGE,"E2.2.0.0");var subQ91=sQuery(id+"F0.wireOp",EDGE,"E2.3.0.0");var subQ92=sQuery(id+"F0.wireOp",EDGE,"E2.4.0.0");var subQ93=sQuery(id+"F0.wireOp",EDGE,"E14.trimOffspring");var subQ94=sQuery(id+"F0.wireOp",EDGE,"E5.trimOffspring");var subQ95=sQuery(id+"F0.wireOp",EDGE,"E15.trimOffspring");var subQ96=sQuery(id+"F0.wireOp",EDGE,"E6.trimOffspring");var subQ97=sQuery(id+"F0.wireOp",EDGE,"E16.trimOffspring");var subQ98=sQuery(id+"F0.wireOp",EDGE,"E7.trimOffspring");var subQ99=sQuery(id+"F0.wireOp",EDGE,"E9.trimOffspring");var subQ100=sQuery(id+"F0.wireOp",EDGE,"E10.trimOffspring");var subQ101=sQuery(id+"F0.wireOp",EDGE,"E22.trimOffspring");var subQ102=sQuery(id+"F0.wireOp",EDGE,"E25.MirrorCS");var subQ103=sQuery(id+"F0.wireOp",EDGE,"E26.MirrorCS");var subQ104=sQuery(id+"F0.wireOp",EDGE,"E17.trimOffspring");var subQ105=sQuery(id+"F0.wireOp",EDGE,"E27.MirrorCS");var subQ106=sQuery(id+"F0.wireOp",EDGE,"E18.trimOffspring");var subQ107=sQuery(id+"F0.wireOp",EDGE,"E19.trimOffspring");var subQ108=sQuery(id+"F0.wireOp",EDGE,"E20.trimOffspring");var subQ109=sQuery(id+"F0.wireOp",EDGE,"E21.trimOffspring");var subQ110=sQuery(id+"F0.wireOp",EDGE,"E23.MirrorCS");var subQ111=sQuery(id+"F0.wireOp",EDGE,"E24.MirrorCS");Q0=makeQuery(id+"F7.boolean.opBoolean","SPLIT",FACE,{"disambiguationData":[TD([subQ18])],"derivedFrom":makeQuery(id+"F3.boolean.opBoolean","SPLIT",FACE,{"disambiguationData":[TD([makeQuery(id+"F1.opExtrude","SWEPT_FACE",FACE,{"disambiguationData":[OSD([subQ85])]})])],"derivedFrom":makeQuery(id+"F1.opExtrude","CAP_FACE",FACE,{"disambiguationData":[OSD([subQ85,subQ81,subQ80,subQ82,subQ88,subQ89,subQ90,subQ91,subQ92,subQ87,subQ79,subQ78,subQ77,subQ76,subQ75,subQ74,subQ73,subQ71,subQ70,subQ69,subQ67,subQ84,subQ94,subQ96,subQ98,subQ72,subQ99,subQ100,subQ68,subQ66,subQ83,subQ93,subQ95,subQ97,subQ104,subQ106,subQ107,subQ108,subQ109,subQ101,subQ110,subQ111,subQ102,subQ103,subQ105,subQ86,subQ65,subQ64,subQ63,subQ62,subQ61,subQ60,subQ59,subQ58,subQ57,subQ56,subQ55,subQ54,subQ53,subQ52,subQ51,subQ50,subQ49,subQ48,subQ47,subQ46,subQ45,subQ44,subQ43,subQ42,subQ41,subQ40,subQ39,subQ38,subQ37,subQ36])],"isStart":false})})});}
            var sketch = newSketch(context, id + "F8", { "sketchPlane" : qUnion([Q0])});
            skLineSegment(sketch, "E67", {"start": v(-13.97, -16.63) * mm, "end": v(-9.02, -9.38) * mm});
            skLineSegment(sketch, "E68", {"start": v(-9.02, -9.38) * mm, "end": v(-8.93, -8.79) * mm});
            skLineSegment(sketch, "E69", {"start": v(-8.93, -8.79) * mm, "end": v(-7.25, -6.91) * mm});
            skLineSegment(sketch, "E70", {"start": v(-7.25, -6.91) * mm, "end": v(-7.25, -3.97) * mm});
            skLineSegment(sketch, "E71", {"start": v(-7.25, -3.97) * mm, "end": v(-8.68, -0.4) * mm});
            skLineSegment(sketch, "E72", {"start": v(-8.68, -0.4) * mm, "end": v(-9.2, -0.02) * mm});
            skLineSegment(sketch, "E73", {"start": v(-9.2, -0.02) * mm, "end": v(-10.11, -0.02) * mm});
            skLineSegment(sketch, "E74", {"start": v(-10.11, -0.02) * mm, "end": v(-12.83, -0.02) * mm});
            skLineSegment(sketch, "E75", {"start": v(-12.83, -0.02) * mm, "end": v(-14.08, 0.65) * mm});
            skLineSegment(sketch, "E76", {"start": v(-14.08, 0.65) * mm, "end": v(-14.38, 1.55) * mm});
            skLineSegment(sketch, "E77", {"start": v(-14.38, 1.55) * mm, "end": v(-14.06, 2.6) * mm});
            skLineSegment(sketch, "E78", {"start": v(-14.06, 2.6) * mm, "end": v(-15.04, 3.77) * mm});
            skLineSegment(sketch, "E79", {"start": v(-15.04, 3.77) * mm, "end": v(-14.78, 4.57) * mm});
            skLineSegment(sketch, "E80", {"start": v(-14.78, 4.57) * mm, "end": v(-15.2, 5.19) * mm});
            skLineSegment(sketch, "E81", {"start": v(-15.2, 5.19) * mm, "end": v(-14.96, 6.55) * mm});
            skLineSegment(sketch, "E82", {"start": v(-14.96, 6.55) * mm, "end": v(-15.4, 6.96) * mm});
            skLineSegment(sketch, "E83", {"start": v(-15.4, 6.96) * mm, "end": v(-16.57, 7.34) * mm});
            skLineSegment(sketch, "E84", {"start": v(-14.09, 11.23) * mm, "end": v(-14.09, 11.72) * mm});
            skLineSegment(sketch, "E85", {"start": v(-14.09, 11.72) * mm, "end": v(-14.53, 12.2) * mm});
            skLineSegment(sketch, "E86", {"start": v(-14.53, 12.2) * mm, "end": v(-14.14, 12.33) * mm});
            skLineSegment(sketch, "E87", {"start": v(-14.14, 12.33) * mm, "end": v(-13.91, 12.21) * mm});
            skLineSegment(sketch, "E88", {"start": v(-13.91, 12.21) * mm, "end": v(-13.91, 12.83) * mm});
            skLineSegment(sketch, "E89", {"start": v(-13.91, 12.83) * mm, "end": v(-14.25, 13.06) * mm});
            skLineSegment(sketch, "E90", {"start": v(-14.25, 13.06) * mm, "end": v(-13.4, 16.24) * mm});
            skLineSegment(sketch, "E91", {"start": v(-13.4, 16.24) * mm, "end": v(-12.48, 17.9) * mm});
            skLineSegment(sketch, "E92", {"start": v(-12.48, 17.9) * mm, "end": v(-12.48, 19.68) * mm});
            skLineSegment(sketch, "E93", {"start": v(-12.48, 19.68) * mm, "end": v(-11.79, 20.82) * mm});
            skLineSegment(sketch, "E94", {"start": v(-11.79, 20.82) * mm, "end": v(-10.37, 21.5) * mm});
            skLineSegment(sketch, "E95", {"start": v(-10.37, 21.5) * mm, "end": v(-9.42, 21.5) * mm});
            skLineSegment(sketch, "E96", {"start": v(-9.42, 21.5) * mm, "end": v(-9.03, 22.35) * mm});
            skLineSegment(sketch, "E97", {"start": v(-9.03, 22.35) * mm, "end": v(-8.44, 22.73) * mm});
            skLineSegment(sketch, "E98", {"start": v(-8.44, 22.73) * mm, "end": v(-8.44, 23.9) * mm});
            skLineSegment(sketch, "E99", {"start": v(-8.44, 23.9) * mm, "end": v(-7.98, 24.4) * mm});
            skLineSegment(sketch, "E100", {"start": v(-7.98, 24.4) * mm, "end": v(-7.85, 25.15) * mm});
            skLineSegment(sketch, "E101", {"start": v(-7.85, 25.15) * mm, "end": v(-6.49, 27.25) * mm});
            skLineSegment(sketch, "E102", {"start": v(-6.49, 27.25) * mm, "end": v(-5.9, 27.25) * mm});
            skLineSegment(sketch, "E103", {"start": v(-5.9, 27.25) * mm, "end": v(-5.76, 26.16) * mm});
            skLineSegment(sketch, "E104", {"start": v(-5.76, 26.16) * mm, "end": v(-6.06, 25.49) * mm});
            skLineSegment(sketch, "E105", {"start": v(-6.06, 25.49) * mm, "end": v(-5.45, 26.02) * mm});
            skLineSegment(sketch, "E106", {"start": v(-5.45, 26.02) * mm, "end": v(-4.96, 26.02) * mm});
            skLineSegment(sketch, "E107", {"start": v(-4.96, 26.02) * mm, "end": v(-4.58, 25.46) * mm});
            skLineSegment(sketch, "E108", {"start": v(-4.58, 25.46) * mm, "end": v(-3.68, 26.6) * mm});
            skLineSegment(sketch, "E109", {"start": v(-3.68, 26.6) * mm, "end": v(-2.88, 26.4) * mm});
            skLineSegment(sketch, "E110", {"start": v(-2.88, 26.4) * mm, "end": v(-2.5, 25.67) * mm});
            skLineSegment(sketch, "E111", {"start": v(-2.5, 25.67) * mm, "end": v(-2.5, 24.67) * mm});
            skLineSegment(sketch, "E112", {"start": v(-2.5, 24.67) * mm, "end": v(-2.08, 24.67) * mm});
            skLineSegment(sketch, "E113", {"start": v(-2.08, 24.67) * mm, "end": v(-1.06, 25.1) * mm});
            skLineSegment(sketch, "E114", {"start": v(-1.06, 25.1) * mm, "end": v(-0.35, 24.53) * mm});
            skLineSegment(sketch, "E115", {"start": v(-0.35, 24.53) * mm, "end": v(-0.35, 23.46) * mm});
            skLineSegment(sketch, "E116", {"start": v(-0.35, 23.46) * mm, "end": v(0.5, 23.46) * mm});
            skLineSegment(sketch, "E117", {"start": v(0.5, 23.46) * mm, "end": v(1.28, 24.5) * mm});
            skLineSegment(sketch, "E118", {"start": v(1.28, 24.5) * mm, "end": v(6.3, 20.91) * mm});
            skLineSegment(sketch, "E119", {"start": v(6.3, 20.91) * mm, "end": v(5.84, 20.21) * mm});
            skLineSegment(sketch, "E120", {"start": v(5.84, 20.21) * mm, "end": v(5.23, 20.04) * mm});
            skLineSegment(sketch, "E121", {"start": v(5.23, 20.04) * mm, "end": v(5.09, 19.58) * mm});
            skLineSegment(sketch, "E122", {"start": v(5.09, 19.58) * mm, "end": v(5.39, 18.58) * mm});
            skLineSegment(sketch, "E123", {"start": v(5.39, 18.58) * mm, "end": v(5.39, 18.28) * mm});
            skLineSegment(sketch, "E124", {"start": v(5.39, 18.28) * mm, "end": v(5.64, 18.28) * mm});
            skLineSegment(sketch, "E125", {"start": v(5.64, 18.28) * mm, "end": v(6.13, 19.06) * mm});
            skLineSegment(sketch, "E126", {"start": v(6.13, 19.06) * mm, "end": v(6.78, 19.16) * mm});
            skLineSegment(sketch, "E127", {"start": v(6.78, 19.16) * mm, "end": v(7.23, 18.93) * mm});
            skLineSegment(sketch, "E128", {"start": v(7.23, 18.93) * mm, "end": v(7.42, 18.32) * mm});
            skLineSegment(sketch, "E129", {"start": v(7.42, 18.32) * mm, "end": v(7.42, 17.75) * mm});
            skLineSegment(sketch, "E130", {"start": v(7.42, 17.75) * mm, "end": v(7.58, 17.75) * mm});
            skLineSegment(sketch, "E131", {"start": v(7.58, 17.75) * mm, "end": v(8.3, 18.47) * mm});
            skLineSegment(sketch, "E132", {"start": v(8.3, 18.47) * mm, "end": v(9.34, 18.47) * mm});
            skLineSegment(sketch, "E133", {"start": v(9.34, 18.47) * mm, "end": v(9.91, 18.12) * mm});
            skLineSegment(sketch, "E134", {"start": v(9.91, 18.12) * mm, "end": v(9.91, 17.45) * mm});
            skLineSegment(sketch, "E135", {"start": v(9.91, 17.45) * mm, "end": v(9.32, 16.94) * mm});
            skLineSegment(sketch, "E136", {"start": v(9.32, 16.94) * mm, "end": v(9.52, 16.51) * mm});
            skLineSegment(sketch, "E137", {"start": v(9.52, 16.51) * mm, "end": v(10.05, 16.65) * mm});
            skLineSegment(sketch, "E138", {"start": v(10.05, 16.65) * mm, "end": v(11.2, 17.62) * mm});
            skLineSegment(sketch, "E139", {"start": v(11.2, 17.62) * mm, "end": v(11.85, 16.88) * mm});
            skLineSegment(sketch, "E140", {"start": v(11.85, 16.88) * mm, "end": v(11.32, 15.8) * mm});
            skLineSegment(sketch, "E141", {"start": v(11.32, 15.8) * mm, "end": v(6.04, 10.75) * mm});
            skLineSegment(sketch, "E142", {"start": v(6.04, 10.75) * mm, "end": v(6.04, 8.87) * mm});
            skLineSegment(sketch, "E143", {"start": v(6.04, 8.87) * mm, "end": v(6.92, 7.78) * mm});
            skLineSegment(sketch, "E144", {"start": v(6.92, 7.78) * mm, "end": v(6.92, 5.74) * mm});
            skLineSegment(sketch, "E145", {"start": v(6.92, 5.74) * mm, "end": v(7.2, 4.99) * mm});
            skLineSegment(sketch, "E146", {"start": v(7.2, 4.99) * mm, "end": v(6.73, 3.92) * mm});
            skLineSegment(sketch, "E147", {"start": v(6.73, 3.92) * mm, "end": v(5.51, 3.45) * mm});
            skLineSegment(sketch, "E148", {"start": v(5.51, 3.45) * mm, "end": v(4.47, 2.04) * mm});
            skLineSegment(sketch, "E149", {"start": v(4.47, 2.04) * mm, "end": v(3.77, 1.83) * mm});
            skLineSegment(sketch, "E150", {"start": v(3.77, 1.83) * mm, "end": v(3.2, 1.94) * mm});
            skLineSegment(sketch, "E151", {"start": v(3.2, 1.94) * mm, "end": v(1.92, 1.38) * mm});
            skLineSegment(sketch, "E152", {"start": v(1.92, 1.38) * mm, "end": v(2.07, -0.23) * mm});
            skLineSegment(sketch, "E153", {"start": v(2.07, -0.23) * mm, "end": v(3.97, -4.39) * mm});
            skLineSegment(sketch, "E154", {"start": v(3.97, -4.39) * mm, "end": v(5.8, -7.08) * mm});
            skLineSegment(sketch, "E155", {"start": v(5.8, -7.08) * mm, "end": v(7.17, -9.46) * mm});
            skLineSegment(sketch, "E156", {"start": v(7.17, -9.46) * mm, "end": v(7.17, -11.73) * mm});
            skLineSegment(sketch, "E157", {"start": v(7.17, -11.73) * mm, "end": v(6.48, -11.73) * mm});
            skLineSegment(sketch, "E158", {"start": v(6.48, -11.73) * mm, "end": v(5.47, -10.86) * mm});
            skLineSegment(sketch, "E159", {"start": v(5.47, -10.86) * mm, "end": v(4.17, -10.86) * mm});
            skLineSegment(sketch, "E160", {"start": v(4.17, -10.86) * mm, "end": v(2.45, -11.18) * mm});
            skLineSegment(sketch, "E161", {"start": v(2.45, -11.18) * mm, "end": v(-9.16, -16.69) * mm});
            skLineSegment(sketch, "E162", {"start": v(-9.16, -16.69) * mm, "end": v(-11.58, -17.32) * mm});
            skLineSegment(sketch, "E163", {"start": v(-11.58, -17.32) * mm, "end": v(-12.91, -17.32) * mm});
            skLineSegment(sketch, "E164", {"start": v(-12.91, -17.32) * mm, "end": v(-13.72, -16.98) * mm});
            skLineSegment(sketch, "E165", {"start": v(-13.72, -16.98) * mm, "end": v(-13.97, -16.63) * mm});
            skLineSegment(sketch, "E166", {"start": v(-16.84, 7.94) * mm, "end": v(-16.84, 7.65) * mm});
            skLineSegment(sketch, "E167", {"start": v(-16.84, 7.65) * mm, "end": v(-16.57, 7.34) * mm});
            skLineSegment(sketch, "E168", {"start": v(-14.09, 11.23) * mm, "end": v(-16.84, 7.94) * mm});
            skSolve(sketch);
        }
        {
            var Q0;
            Q0=makeQuery(id+"F8.imprint","IMPRINT",FACE,{"disambiguationData":[TD([[makeQuery(id+"F8.imprint","IMPRINT",EDGE,{"derivedFrom":sQuery(id+"F8.wireOp",EDGE,"E67")}),-1.0]])]});
            var Q1;
            Q1=sQuery(id+"F8.wireOp",EDGE,"E161");
            var Q2;
            Q2=sQuery(id+"F8.wireOp",EDGE,"E141");
            var Q3;
            Q3=sQuery(id+"F8.wireOp",EDGE,"E118");
            var Q4;
            Q4=sQuery(id+"F8.wireOp",EDGE,"E67");
            var Q5;
            Q5=sQuery(id+"F8.wireOp",EDGE,"E113");
            var Q6;
            Q6=sQuery(id+"F8.wireOp",EDGE,"E115");
            var Q7;
            Q7=sQuery(id+"F8.wireOp",EDGE,"E163");
            var Q8;
            Q8=sQuery(id+"F8.wireOp",EDGE,"E147");
            var Q9;
            Q9=sQuery(id+"F8.wireOp",EDGE,"E114");
            var Q10;
            Q10=sQuery(id+"F8.wireOp",EDGE,"E98");
            var Q11;
            Q11=sQuery(id+"F8.wireOp",EDGE,"E162");
            var Q12;
            Q12=sQuery(id+"F8.wireOp",EDGE,"E145");
            var Q13;
            Q13=sQuery(id+"F8.wireOp",EDGE,"E168");
            var Q14;
            Q14=sQuery(id+"F8.wireOp",EDGE,"E152");
            var Q15;
            Q15=sQuery(id+"F8.wireOp",EDGE,"E97");
            var Q16;
            Q16=sQuery(id+"F8.wireOp",EDGE,"E143");
            var Q17;
            Q17=sQuery(id+"F8.wireOp",EDGE,"E95");
            var Q18;
            Q18=sQuery(id+"F8.wireOp",EDGE,"E151");
            var Q19;
            Q19=sQuery(id+"F8.wireOp",EDGE,"E144");
            var Q20;
            Q20=sQuery(id+"F8.wireOp",EDGE,"E155");
            var Q21;
            Q21=sQuery(id+"F8.wireOp",EDGE,"E94");
            var Q22;
            Q22=sQuery(id+"F8.wireOp",EDGE,"E112");
            var Q23;
            Q23=sQuery(id+"F8.wireOp",EDGE,"E96");
            var Q24;
            Q24=sQuery(id+"F8.wireOp",EDGE,"E157");
            var Q25;
            Q25=sQuery(id+"F8.wireOp",EDGE,"E158");
            var Q26;
            Q26=sQuery(id+"F8.wireOp",EDGE,"E93");
            var Q27;
            Q27=sQuery(id+"F8.wireOp",EDGE,"E142");
            var Q28;
            Q28=sQuery(id+"F8.wireOp",EDGE,"E77");
            var Q29;
            Q29=sQuery(id+"F8.wireOp",EDGE,"E75");
            var Q30;
            Q30=sQuery(id+"F8.wireOp",EDGE,"E74");
            var Q31;
            Q31=sQuery(id+"F8.wireOp",EDGE,"E78");
            var Q32;
            Q32=sQuery(id+"F8.wireOp",EDGE,"E73");
            var Q33;
            Q33=sQuery(id+"F8.wireOp",EDGE,"E76");
            var Q34;
            Q34=sQuery(id+"F8.wireOp",EDGE,"E150");
            var Q35;
            Q35=sQuery(id+"F8.wireOp",EDGE,"E68");
            var Q36;
            Q36=sQuery(id+"F8.wireOp",EDGE,"E156");
            var Q37;
            Q37=sQuery(id+"F8.wireOp",EDGE,"E72");
            var Q38;
            Q38=sQuery(id+"F8.wireOp",EDGE,"E71");
            var Q39;
            Q39=sQuery(id+"F8.wireOp",EDGE,"E92");
            var Q40;
            Q40=sQuery(id+"F8.wireOp",EDGE,"E70");
            var Q41;
            Q41=sQuery(id+"F8.wireOp",EDGE,"E116");
            var Q42;
            Q42=sQuery(id+"F8.wireOp",EDGE,"E140");
            var Q43;
            Q43=sQuery(id+"F8.wireOp",EDGE,"E69");
            var Q44;
            Q44=sQuery(id+"F8.wireOp",EDGE,"E91");
            var Q45;
            Q45=sQuery(id+"F8.wireOp",EDGE,"E117");
            var Q46;
            Q46=sQuery(id+"F8.wireOp",EDGE,"E139");
            var Q47;
            Q47=sQuery(id+"F8.wireOp",EDGE,"E149");
            var Q48;
            Q48=sQuery(id+"F8.wireOp",EDGE,"E99");
            var Q49;
            Q49=sQuery(id+"F8.wireOp",EDGE,"E146");
            var Q50;
            Q50=sQuery(id+"F8.wireOp",EDGE,"E153");
            var Q51;
            Q51=sQuery(id+"F8.wireOp",EDGE,"E90");
            var Q52;
            Q52=sQuery(id+"F8.wireOp",EDGE,"E148");
            var Q53;
            Q53=sQuery(id+"F8.wireOp",EDGE,"E100");
            var Q54;
            Q54=sQuery(id+"F8.wireOp",EDGE,"E164");
            var Q55;
            Q55=sQuery(id+"F8.wireOp",EDGE,"E154");
            var Q56;
            Q56=sQuery(id+"F8.wireOp",EDGE,"E101");
            var Q57;
            Q57=sQuery(id+"F8.wireOp",EDGE,"E165");
            var Q58;
            Q58=sQuery(id+"F8.wireOp",EDGE,"E83");
            var Q59;
            Q59=sQuery(id+"F8.wireOp",EDGE,"E137");
            var Q60;
            Q60=sQuery(id+"F8.wireOp",EDGE,"E88");
            var Q61;
            Q61=sQuery(id+"F8.wireOp",EDGE,"E120");
            var Q62;
            Q62=sQuery(id+"F8.wireOp",EDGE,"E104");
            var Q63;
            Q63=sQuery(id+"F8.wireOp",EDGE,"E159");
            var Q64;
            Q64=sQuery(id+"F8.wireOp",EDGE,"E111");
            var Q65;
            Q65=sQuery(id+"F8.wireOp",EDGE,"E119");
            var Q66;
            Q66=sQuery(id+"F8.wireOp",EDGE,"E160");
            var Q67;
            Q67=sQuery(id+"F8.wireOp",EDGE,"E103");
            var Q68;
            Q68=sQuery(id+"F8.wireOp",EDGE,"E167");
            var Q69;
            Q69=sQuery(id+"F8.wireOp",EDGE,"E110");
            var Q70;
            Q70=sQuery(id+"F8.wireOp",EDGE,"E126");
            var Q71;
            Q71=sQuery(id+"F8.wireOp",EDGE,"E134");
            var Q72;
            Q72=sQuery(id+"F8.wireOp",EDGE,"E86");
            var Q73;
            Q73=sQuery(id+"F8.wireOp",EDGE,"E102");
            var Q74;
            Q74=sQuery(id+"F8.wireOp",EDGE,"E123");
            var Q75;
            Q75=sQuery(id+"F8.wireOp",EDGE,"E166");
            var Q76;
            Q76=sQuery(id+"F8.wireOp",EDGE,"E109");
            var Q77;
            Q77=sQuery(id+"F8.wireOp",EDGE,"E79");
            var Q78;
            Q78=sQuery(id+"F8.wireOp",EDGE,"E89");
            var Q79;
            Q79=sQuery(id+"F8.wireOp",EDGE,"E108");
            var Q80;
            Q80=sQuery(id+"F8.wireOp",EDGE,"E81");
            var Q81;
            Q81=sQuery(id+"F8.wireOp",EDGE,"E80");
            var Q82;
            Q82=sQuery(id+"F8.wireOp",EDGE,"E107");
            var Q83;
            Q83=sQuery(id+"F8.wireOp",EDGE,"E121");
            var Q84;
            Q84=sQuery(id+"F8.wireOp",EDGE,"E105");
            var Q85;
            Q85=sQuery(id+"F8.wireOp",EDGE,"E138");
            var Q86;
            Q86=sQuery(id+"F8.wireOp",EDGE,"E122");
            var Q87;
            Q87=sQuery(id+"F8.wireOp",EDGE,"E84");
            var Q88;
            Q88=sQuery(id+"F8.wireOp",EDGE,"E131");
            var Q89;
            Q89=sQuery(id+"F8.wireOp",EDGE,"E136");
            var Q90;
            Q90=sQuery(id+"F8.wireOp",EDGE,"E129");
            var Q91;
            Q91=sQuery(id+"F8.wireOp",EDGE,"E127");
            var Q92;
            Q92=sQuery(id+"F8.wireOp",EDGE,"E87");
            var Q93;
            Q93=sQuery(id+"F8.wireOp",EDGE,"E135");
            var Q94;
            Q94=sQuery(id+"F8.wireOp",EDGE,"E125");
            var Q95;
            Q95=sQuery(id+"F8.wireOp",EDGE,"E82");
            var Q96;
            Q96=sQuery(id+"F8.wireOp",EDGE,"E85");
            var Q97;
            Q97=sQuery(id+"F8.wireOp",EDGE,"E132");
            var Q98;
            Q98=sQuery(id+"F8.wireOp",EDGE,"E133");
            var Q99;
            Q99=sQuery(id+"F8.wireOp",EDGE,"E106");
            var Q100;
            Q100=sQuery(id+"F8.wireOp",EDGE,"E130");
            var Q101;
            Q101=sQuery(id+"F8.wireOp",EDGE,"E128");
            var Q102;
            Q102=sQuery(id+"F8.wireOp",EDGE,"E124");
            extrude(context, id + "F9", {"entities" : qUnion([Q0]), "surfaceEntities" : qUnion([Q1, Q2, Q3, Q4, Q5, Q6, Q7, Q8, Q9, Q10, Q11, Q12, Q13, Q14, Q15, Q16, Q17, Q18, Q19, Q20, Q21, Q22, Q23, Q24, Q25, Q26, Q27, Q28, Q29, Q30, Q31, Q32, Q33, Q34, Q35, Q36, Q37, Q38, Q39, Q40, Q41, Q42, Q43, Q44, Q45, Q46, Q47, Q48, Q49, Q50, Q51, Q52, Q53, Q54, Q55, Q56, Q57, Q58, Q59, Q60, Q61, Q62, Q63, Q64, Q65, Q66, Q67, Q68, Q69, Q70, Q71, Q72, Q73, Q74, Q75, Q76, Q77, Q78, Q79, Q80, Q81, Q82, Q83, Q84, Q85, Q86, Q87, Q88, Q89, Q90, Q91, Q92, Q93, Q94, Q95, Q96, Q97, Q98, Q99, Q100, Q101, Q102]), "depth" : 2 * mm});
        }
        {
            var Q0;
            Q0=makeQuery(id+"F9.opExtrude","SWEPT_BODY",BODY,{"disambiguationData":[OSD([sQuery(id+"F8.wireOp",EDGE,"E67"),sQuery(id+"F8.wireOp",EDGE,"E68"),sQuery(id+"F8.wireOp",EDGE,"E69"),sQuery(id+"F8.wireOp",EDGE,"E70"),sQuery(id+"F8.wireOp",EDGE,"E71"),sQuery(id+"F8.wireOp",EDGE,"E72"),sQuery(id+"F8.wireOp",EDGE,"E73"),sQuery(id+"F8.wireOp",EDGE,"E74"),sQuery(id+"F8.wireOp",EDGE,"E75"),sQuery(id+"F8.wireOp",EDGE,"E76"),sQuery(id+"F8.wireOp",EDGE,"E77"),sQuery(id+"F8.wireOp",EDGE,"E78"),sQuery(id+"F8.wireOp",EDGE,"E79"),sQuery(id+"F8.wireOp",EDGE,"E80"),sQuery(id+"F8.wireOp",EDGE,"E81"),sQuery(id+"F8.wireOp",EDGE,"E82"),sQuery(id+"F8.wireOp",EDGE,"E83"),sQuery(id+"F8.wireOp",EDGE,"E84"),sQuery(id+"F8.wireOp",EDGE,"E85"),sQuery(id+"F8.wireOp",EDGE,"E86"),sQuery(id+"F8.wireOp",EDGE,"E87"),sQuery(id+"F8.wireOp",EDGE,"E88"),sQuery(id+"F8.wireOp",EDGE,"E89"),sQuery(id+"F8.wireOp",EDGE,"E90"),sQuery(id+"F8.wireOp",EDGE,"E91"),sQuery(id+"F8.wireOp",EDGE,"E92"),sQuery(id+"F8.wireOp",EDGE,"E93"),sQuery(id+"F8.wireOp",EDGE,"E94"),sQuery(id+"F8.wireOp",EDGE,"E95"),sQuery(id+"F8.wireOp",EDGE,"E96"),sQuery(id+"F8.wireOp",EDGE,"E97"),sQuery(id+"F8.wireOp",EDGE,"E98"),sQuery(id+"F8.wireOp",EDGE,"E99"),sQuery(id+"F8.wireOp",EDGE,"E100"),sQuery(id+"F8.wireOp",EDGE,"E101"),sQuery(id+"F8.wireOp",EDGE,"E102"),sQuery(id+"F8.wireOp",EDGE,"E103"),sQuery(id+"F8.wireOp",EDGE,"E104"),sQuery(id+"F8.wireOp",EDGE,"E105"),sQuery(id+"F8.wireOp",EDGE,"E106"),sQuery(id+"F8.wireOp",EDGE,"E107"),sQuery(id+"F8.wireOp",EDGE,"E108"),sQuery(id+"F8.wireOp",EDGE,"E109"),sQuery(id+"F8.wireOp",EDGE,"E110"),sQuery(id+"F8.wireOp",EDGE,"E111"),sQuery(id+"F8.wireOp",EDGE,"E112"),sQuery(id+"F8.wireOp",EDGE,"E113"),sQuery(id+"F8.wireOp",EDGE,"E114"),sQuery(id+"F8.wireOp",EDGE,"E115"),sQuery(id+"F8.wireOp",EDGE,"E116"),sQuery(id+"F8.wireOp",EDGE,"E117"),sQuery(id+"F8.wireOp",EDGE,"E118"),sQuery(id+"F8.wireOp",EDGE,"E119"),sQuery(id+"F8.wireOp",EDGE,"E120"),sQuery(id+"F8.wireOp",EDGE,"E121"),sQuery(id+"F8.wireOp",EDGE,"E122"),sQuery(id+"F8.wireOp",EDGE,"E123"),sQuery(id+"F8.wireOp",EDGE,"E124"),sQuery(id+"F8.wireOp",EDGE,"E125"),sQuery(id+"F8.wireOp",EDGE,"E126"),sQuery(id+"F8.wireOp",EDGE,"E127"),sQuery(id+"F8.wireOp",EDGE,"E128"),sQuery(id+"F8.wireOp",EDGE,"E129"),sQuery(id+"F8.wireOp",EDGE,"E130"),sQuery(id+"F8.wireOp",EDGE,"E131"),sQuery(id+"F8.wireOp",EDGE,"E132"),sQuery(id+"F8.wireOp",EDGE,"E133"),sQuery(id+"F8.wireOp",EDGE,"E134"),sQuery(id+"F8.wireOp",EDGE,"E135"),sQuery(id+"F8.wireOp",EDGE,"E136"),sQuery(id+"F8.wireOp",EDGE,"E137"),sQuery(id+"F8.wireOp",EDGE,"E138"),sQuery(id+"F8.wireOp",EDGE,"E139"),sQuery(id+"F8.wireOp",EDGE,"E140"),sQuery(id+"F8.wireOp",EDGE,"E141"),sQuery(id+"F8.wireOp",EDGE,"E142"),sQuery(id+"F8.wireOp",EDGE,"E143"),sQuery(id+"F8.wireOp",EDGE,"E144"),sQuery(id+"F8.wireOp",EDGE,"E145"),sQuery(id+"F8.wireOp",EDGE,"E146"),sQuery(id+"F8.wireOp",EDGE,"E147"),sQuery(id+"F8.wireOp",EDGE,"E148"),sQuery(id+"F8.wireOp",EDGE,"E149"),sQuery(id+"F8.wireOp",EDGE,"E150"),sQuery(id+"F8.wireOp",EDGE,"E151"),sQuery(id+"F8.wireOp",EDGE,"E152"),sQuery(id+"F8.wireOp",EDGE,"E153"),sQuery(id+"F8.wireOp",EDGE,"E154"),sQuery(id+"F8.wireOp",EDGE,"E155"),sQuery(id+"F8.wireOp",EDGE,"E156"),sQuery(id+"F8.wireOp",EDGE,"E157"),sQuery(id+"F8.wireOp",EDGE,"E158"),sQuery(id+"F8.wireOp",EDGE,"E159"),sQuery(id+"F8.wireOp",EDGE,"E160"),sQuery(id+"F8.wireOp",EDGE,"E161"),sQuery(id+"F8.wireOp",EDGE,"E162"),sQuery(id+"F8.wireOp",EDGE,"E163"),sQuery(id+"F8.wireOp",EDGE,"E164"),sQuery(id+"F8.wireOp",EDGE,"E165"),sQuery(id+"F8.wireOp",EDGE,"E166"),sQuery(id+"F8.wireOp",EDGE,"E167"),sQuery(id+"F8.wireOp",EDGE,"E168")])]});
            transform(context, id + "F10", {"entities" : qUnion([Q0]), "transformType" : TransformType.TRANSLATION_3D, "dx" : 4.4 * mm, "dy" : -1.5 * mm, "dz" : 0 * mm, "makeCopy" : false});
        }
    });
